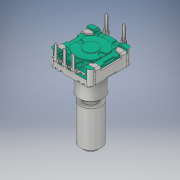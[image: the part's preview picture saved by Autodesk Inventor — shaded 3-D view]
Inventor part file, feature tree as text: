
AUTODESK INVENTOR PART (.ipt)
format: ipt  version: 2018 (Build 220112000, 112)  size: 723,456 bytes
history: native  units: mm
features: plane x2, extrude x2, sketch x2
ambient origin geometry x8: Origin, YZ Plane, XZ Plane, XY Plane, X Axis, Y Axis, Z Axis, Center Point
bodies: Volumenkörper1 (feature_tree)
feature tree (6):
  plane  "Arbeitsebene2"
  extrude  "Extrusion1"  Depth=2.17mm TaperAngle=0.0deg
  plane  "Arbeitsebene3"
  extrude  "Extrusion2"  Depth=3.43mm TaperAngle=0.0deg
  sketch  "Skizze1"  dims[d0=1.75mm d1=2.17mm d2=0.0mm]
  sketch  "Skizze2"  dims[d3=3.0mm d4=3.43mm d5=0.0mm]
